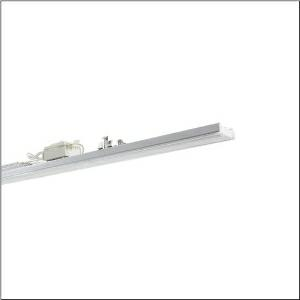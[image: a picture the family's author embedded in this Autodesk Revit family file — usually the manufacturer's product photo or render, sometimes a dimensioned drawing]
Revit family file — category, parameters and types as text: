
# Revit family: licross_r__21_recessed_mo_52te14cn485g_c326
name_source: partatom
category: Lighting Fixtures
units: mm (PartAtom-declared; Revit-internal decimal feet)

## family parameters
Cut with Voids When Loaded = No
Host = Face
Light Source = No
Part Type = Normal
Room Calculation Point = No
Round Connector Dimension = Use Diameter
Shared = No

## types (1)
- --- (1 x LED, 8530 lm, 49.9 W, 4000K)
    Apparent Load = 50 VA
    CIE Flux Codes = 56 84 97 100 100
    Color Rendering = 80
    Color Temperature = 4000K
    Default Elevation = 1800 mm
    Description = Licross® 21 Recessed MO, luminaire insert, of sheet steel, galvanised, coil coated, white, length: 1.500mm, width: 66mm, height: 67mm, LED rated luminous flux: 8.530lm, light colour: 840, control gear: ON/OFF Multilumen, CLOi, control gear: ECG DALI, with plug, 5-pole, with phase selection, mains connection: 220..240V, AC, 50/60Hz, start of lifetime: 50W, end of service life: 61W, halogen-free wiring, primary light control with lens, of plastic, primary optical cover: cover, of PMMA, light emission: direct distribution, primary light characteristic: asymmetric, protection rating (complete): IP54, insulation class (complete): insulation class I (protective earthing), certification: CE, ENEC, VDE, UKCA, protection symbol: D if used in an environment with non-conductive dust loads with corresponding accessories, impact resistance: IK06, permissible ambient temperature for indoor applications: -35..+40°C, corresponds to IFS (International Featured Standards) requirements for safety and quality in the food industry, reducing of maximum allowable ambient temperature of 5°C with ceiling mounting, LABS conformity tested according to VDMA 24364:2018-05, packaging unit: 1 piece
    Height = 58 mm
    Lamp = 1 x LED
    Lamp Light Flux = 8530 lm
    Lamp Power = 49.9 W
    Lamp count = 1
    Length = 1500 mm
    Luminous efficacy = 171 lm/W
    Manufacturer = Siteco
    ModVariant = No
    Model = 52TE14CN485G
    Mounting Place = Ceiling
    Mounting Type = Pendant
    Number of Poles = 1
    OnlyDefault = Yes
    Power Factor = 1
    Product Name = Licross® 21 Recessed MO
    Product group = luminaire insert
    ProductGroupID = 902
    Protection Class = Protection class I
    Protection Degree = IP 54
    RLX_Detail_Level = 1
    RLX_Emergency_Light_Flux = 0 lm
    RLX_Emergency_Type = 0
    RLX_Emergency_Type_DB = No
    RlxData = <blob elided: 22789 chars, md5=8cca2421>
    Socket = socket
    Standby Power = 0 W
    System Light Flux = 8530 lm
    System Power = 50 W
    Type Comments = factory setting: luminous flux: 100 % | (A | C | E) | 116 mA
    Type Image = l_1296930.jpg
    URL = http://relux.com
    VarID = @adj_110766
    Voltage = 0 V
    Weight = 0.00 kg
    Width = 66 mm

## geometry (parser evidence)
native form markers: Blend x4, Sweep x12
no freeform markers — native parametric forms only
